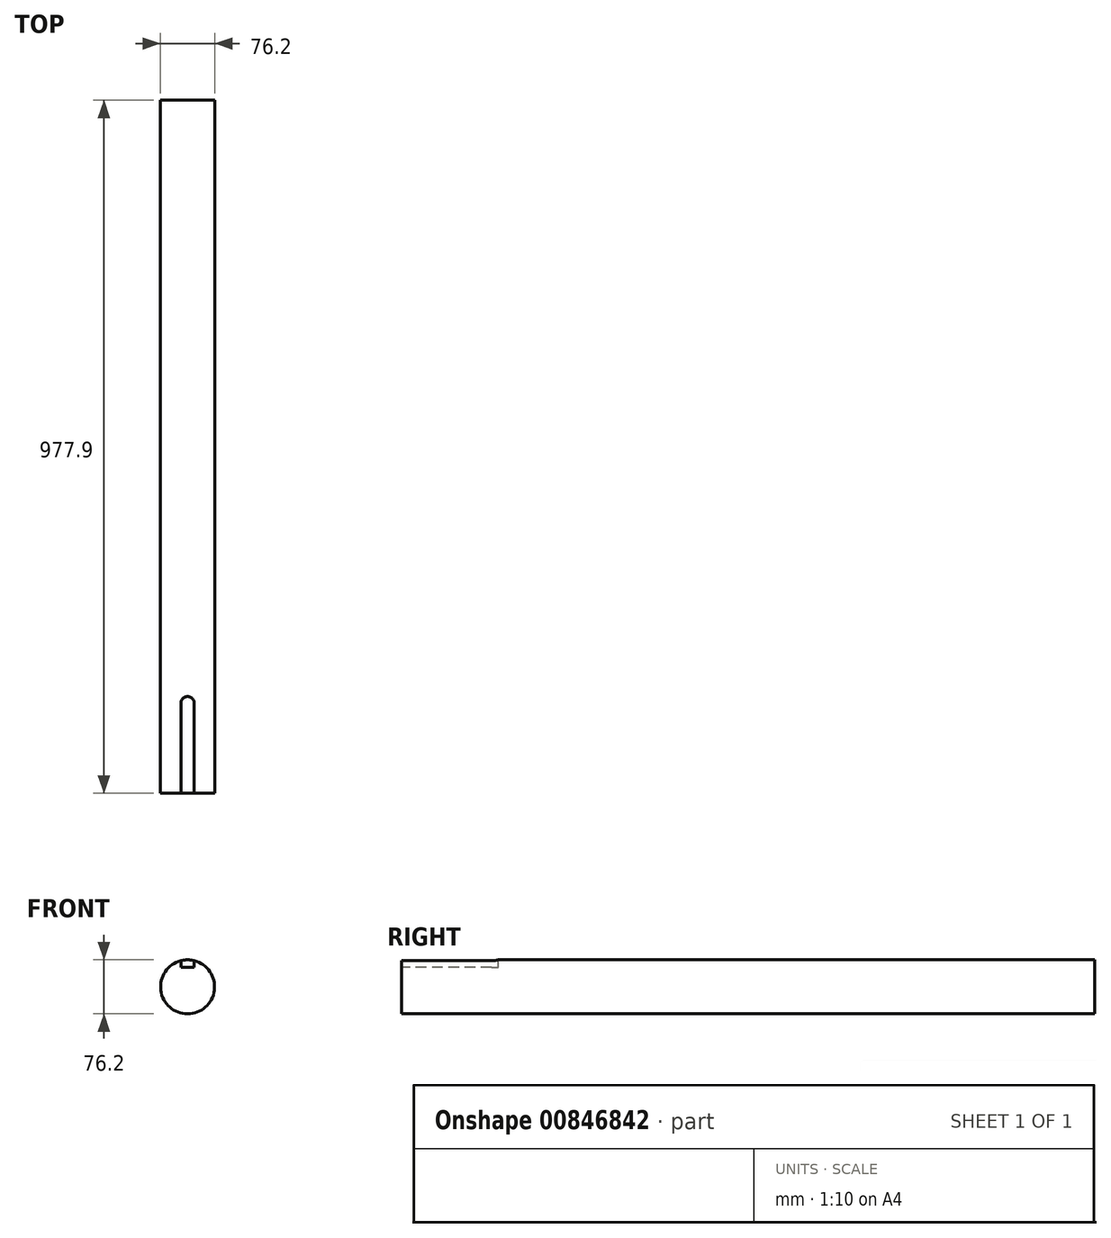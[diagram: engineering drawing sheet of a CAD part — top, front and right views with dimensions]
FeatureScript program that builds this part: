
annotation { "Feature Type Name" : "Feature", "Feature Type Description" : "" }
export const myFeature = defineFeature(function(context is Context, id is Id, definition is map)
    precondition{}
    {
        {
            var Q0;
            Q0=qCreatedBy(makeId("Front.planeOp"),FACE);
            var sketch = newSketch(context, id + "F0", { "sketchPlane" : qUnion([Q0])});
            skCircle(sketch, "E0", {"center": v(0, 0) * mm, "radius": 38.1 * mm});
            skSolve(sketch);
        }
        {
            var Q0;
            Q0=makeQuery(id+"F0.imprint","IMPRINT",FACE,{"disambiguationData":[TD([[makeQuery(id+"F0.imprint","IMPRINT",EDGE,{"derivedFrom":sQuery(id+"F0.wireOp",EDGE,"E0")}),1.0]])]});
            extrude(context, id + "F1", {"entities" : qUnion([Q0]), "depth" : 977.9 * mm, "offsetDistance" : 25.4 * mm, "symmetric" : true});
        }
        {
            var Q0;
            Q0=qCreatedBy(makeId("Top.planeOp"),FACE);
            cPlane(context, id + "F2", {"entities" : qUnion([Q0]), "cplaneType" : CPlaneType.OFFSET, "offset" : 38.1 * mm, "width" : 152.4 * mm, "height" : 152.4 * mm});
        }
        {
            var Q0;
            Q0=qCreatedBy(id+"F2.planeOp",FACE);
            var sketch = newSketch(context, id + "F3", { "sketchPlane" : qUnion([Q0])});
            skLineSegment(sketch, "E1.bottom", {"start": v(-9.53, -361.95) * mm, "end": v(9.53, -361.95) * mm, "construction": true});
            skLineSegment(sketch, "E1.top", {"start": v(-9.52, -574.18) * mm, "end": v(9.52, -574.18) * mm});
            skLineSegment(sketch, "E1.left", {"start": v(-9.53, -361.95) * mm, "end": v(-9.53, -574.18) * mm});
            skLineSegment(sketch, "E1.right", {"start": v(9.52, -361.95) * mm, "end": v(9.52, -574.18) * mm});
            skArc(sketch, "E2", {"start": v(9.53, -361.95) * mm, "mid": v(0, -352.43) * mm, "end": v(-9.52, -361.95) * mm});
            skLineSegment(sketch, "E3", {"start": v(0, 0) * mm, "end": v(0, -361.95) * mm, "construction": true});
            skSolve(sketch);
        }
        {
            var Q0;
            Q0 = qSketchRegion(id + "F3", true);
            extrude(context, id + "F4", {"entities" : qUnion([Q0]), "operationType" : NewBodyOperationType.REMOVE, "oppositeDirection" : true, "depth" : 10.74 * mm, "offsetDistance" : 25.4 * mm});
        }
    });
